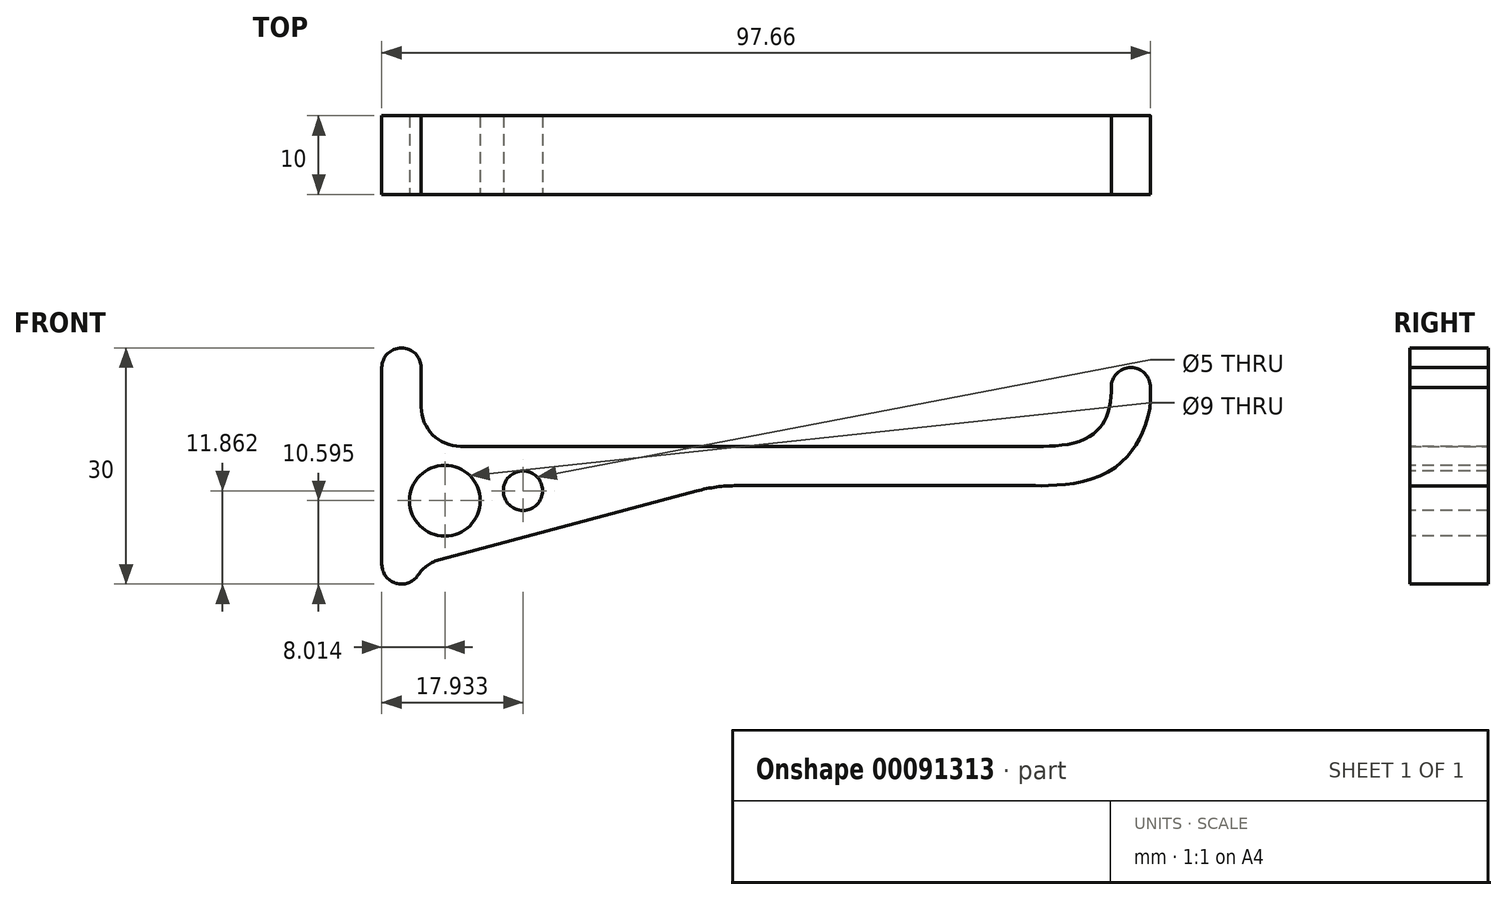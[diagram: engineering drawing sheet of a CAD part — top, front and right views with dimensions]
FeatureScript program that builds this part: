
annotation { "Feature Type Name" : "Feature", "Feature Type Description" : "" }
export const myFeature = defineFeature(function(context is Context, id is Id, definition is map)
    precondition{}
    {
        {
            var Q0;
            Q0=qCreatedBy(makeId("Front.planeOp"),FACE);
            var sketch = newSketch(context, id + "F0", { "sketchPlane" : qUnion([Q0])});
            skLineSegment(sketch, "E0", {"start": v(-40, 0) * mm, "end": v(40, 0) * mm});
            skLineSegment(sketch, "E1", {"start": v(-40, 12.5) * mm, "end": v(-40, -12.5) * mm});
            skFitSpline(sketch, "E2", {"points": [v(40, 0) * mm, v(52.65, 10) * mm], "startDerivative": vector(12.88, 0) * mm, "endDerivative": vector(0, 30) * mm});
            skArc(sketch, "E3.0.startCap", {"start": v(-40, -2.5) * mm, "mid": v(-42.5, 0) * mm, "end": v(-40, 2.5) * mm});
            skArc(sketch, "E3.0.endCap", {"start": v(40, 2.5) * mm, "mid": v(42.5, 0) * mm, "end": v(40, -2.5) * mm});
            skLineSegment(sketch, "E3.0.left", {"start": v(-40, 2.5) * mm, "end": v(40, 2.5) * mm});
            skLineSegment(sketch, "E3.0.right", {"start": v(-40, -2.5) * mm, "end": v(40, -2.5) * mm});
            skArc(sketch, "E3.1.startCap", {"start": v(-42.5, 12.5) * mm, "mid": v(-40, 15) * mm, "end": v(-37.5, 12.5) * mm});
            skArc(sketch, "E3.1.endCap", {"start": v(-37.5, -12.5) * mm, "mid": v(-40, -15) * mm, "end": v(-42.5, -12.5) * mm});
            skLineSegment(sketch, "E3.1.left", {"start": v(-37.5, 12.5) * mm, "end": v(-37.5, -12.5) * mm});
            skLineSegment(sketch, "E3.1.right", {"start": v(-42.5, 12.5) * mm, "end": v(-42.5, -12.5) * mm});
            skArc(sketch, "E3.2.startCap", {"start": v(40, -2.5) * mm, "mid": v(37.5, 0) * mm, "end": v(40, 2.5) * mm});
            skArc(sketch, "E3.2.endCap", {"start": v(50.15, 10) * mm, "mid": v(52.65, 12.5) * mm, "end": v(55.15, 10) * mm});
            skFitSpline(sketch, "E3.2.left", {"points": [v(40, 2.5) * mm, v(40.54, 2.5) * mm, v(41.68, 2.5) * mm, v(43.51, 2.6) * mm, v(45.31, 2.9) * mm, v(46.91, 3.46) * mm, v(47.98, 4.14) * mm, v(48.69, 4.85) * mm, v(49.15, 5.49) * mm, v(49.55, 6.28) * mm, v(49.98, 7.59) * mm, v(50.15, 8.92) * mm, v(50.15, 10) * mm]});
            skFitSpline(sketch, "E3.2.right", {"points": [v(40, -2.5) * mm, v(40.54, -2.5) * mm, v(41.8, -2.5) * mm, v(44.03, -2.37) * mm, v(46.48, -1.97) * mm, v(49.02, -1.12) * mm, v(51.07, 0.15) * mm, v(52.51, 1.6) * mm, v(53.45, 2.9) * mm, v(54.2, 4.39) * mm, v(54.93, 6.63) * mm, v(55.15, 8.58) * mm, v(55.15, 10) * mm]});
            skLineSegment(sketch, "E4", {"start": v(0, 0) * mm, "end": v(0, -2.5) * mm, "construction": true});
            skLineSegment(sketch, "E5", {"start": v(-37.5, -12.5) * mm, "end": v(0, -2.5) * mm});
            skSolve(sketch);
        }
        {
            var Q0;
            Q0 = qSketchRegion(id + "F0", true);
            var Q1;
            {var subQ0=sQuery(id+"F0.wireOp",EDGE,"E1");var subQ1=sQuery(id+"F0.wireOp",EDGE,"E0");var subQ2=makeQuery(id+"F0.imprint","INTERSECT",VERTEX,{"derivedFrom":[subQ1,subQ0]});Q1=makeQuery(id+"F0.imprint","IMPRINT",FACE,{"disambiguationData":[TD([[makeQuery(id+"F0.imprint","IMPRINT",EDGE,{"disambiguationData":[TD([[subQ2,-1.0]])],"derivedFrom":subQ1}),-1.0]])]});}
            extrude(context, id + "F1", {"entities" : qUnion([Q0, Q1]), "depth" : 10 * mm});
        }
        {
            var Q0;
            Q0=makeQuery(id+"F1.opExtrude","SWEPT_EDGE",EDGE,{"disambiguationData":[OSD([sQuery(id+"F0.wireOp",EDGE,"E3.1.endCap"),sQuery(id+"F0.wireOp",EDGE,"E3.1.left"),sQuery(id+"F0.wireOp",EDGE,"E5")])]});
            var Q1;
            Q1=makeQuery(id+"F1.opExtrude","SWEPT_EDGE",EDGE,{"disambiguationData":[OSD([sQuery(id+"F0.wireOp",EDGE,"E3.0.left"),sQuery(id+"F0.wireOp",EDGE,"E3.1.left")])]});
            fillet(context, id + "F2", {"entities" : qUnion([Q0, Q1]), "radius" : 5 * mm, "tangentPropagation" : true, "allowEdgeOverflow" : false});
        }
        {
            var Q0;
            Q0=makeQuery(id+"F1.opExtrude","CAP_FACE",FACE,{"disambiguationData":[OSD([sQuery(id+"F0.wireOp",EDGE,"E3.0.left"),sQuery(id+"F0.wireOp",EDGE,"E3.0.right"),sQuery(id+"F0.wireOp",EDGE,"E3.1.startCap"),sQuery(id+"F0.wireOp",EDGE,"E3.1.endCap"),sQuery(id+"F0.wireOp",EDGE,"E3.1.left"),sQuery(id+"F0.wireOp",EDGE,"E3.1.right"),sQuery(id+"F0.wireOp",EDGE,"E3.2.endCap"),sQuery(id+"F0.wireOp",EDGE,"E3.2.left"),sQuery(id+"F0.wireOp",EDGE,"E3.2.right"),sQuery(id+"F0.wireOp",EDGE,"E5")])],"isStart":false});
            var sketch = newSketch(context, id + "F3", { "sketchPlane" : qUnion([Q0])});
            skCircle(sketch, "E6", {"center": v(-34.49, -4.4) * mm, "radius": 4.5 * mm});
            skCircle(sketch, "E7", {"center": v(-24.57, -3.14) * mm, "radius": 2.5 * mm});
            skLineSegment(sketch, "E8", {"start": v(-42.5, -5.43) * mm, "end": v(0, 0) * mm});
            skSolve(sketch);
        }
        {
            var Q0;
            Q0 = qSketchRegion(id + "F3", true);
            extrude(context, id + "F4", {"entities" : qUnion([Q0]), "operationType" : NewBodyOperationType.REMOVE, "oppositeDirection" : true, "depth" : 25 * mm});
        }
        {
            var Q0;
            Q0=makeQuery(id+"F1.opExtrude","SWEPT_EDGE",EDGE,{"disambiguationData":[OSD([sQuery(id+"F0.wireOp",EDGE,"E3.0.right"),sQuery(id+"F0.wireOp",EDGE,"E5")])]});
            fillet(context, id + "F5", {"entities" : qUnion([Q0]), "radius" : 20 * mm, "tangentPropagation" : true, "allowEdgeOverflow" : false});
        }
    });
